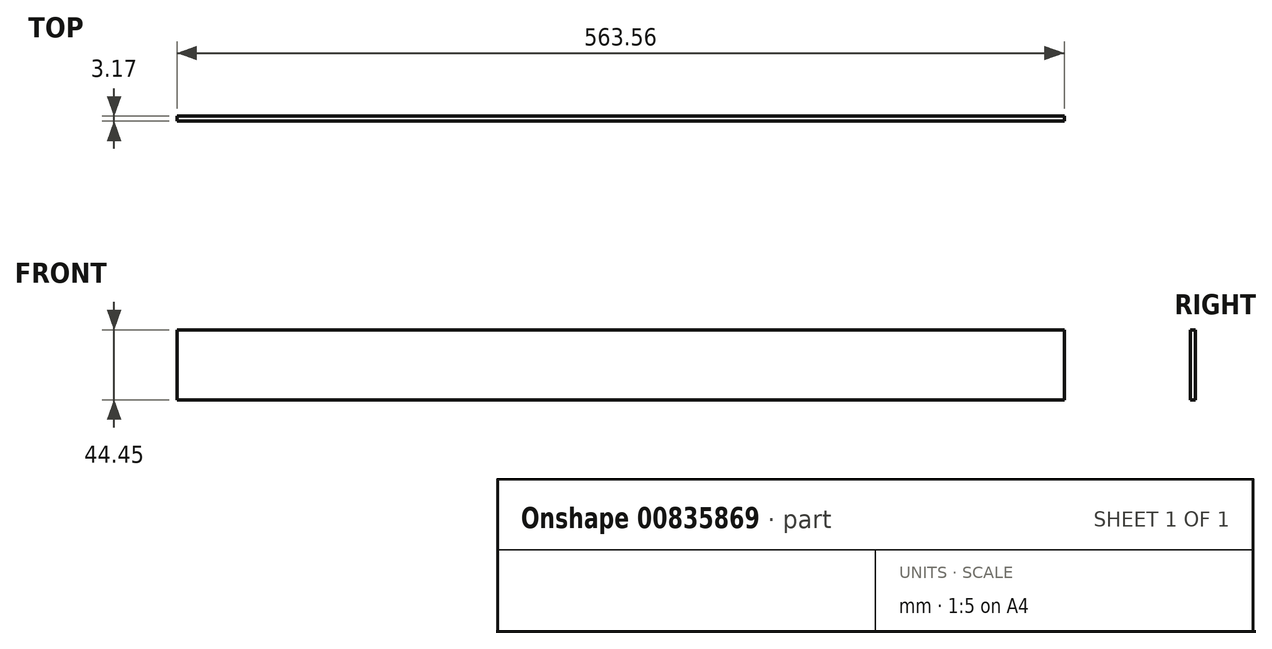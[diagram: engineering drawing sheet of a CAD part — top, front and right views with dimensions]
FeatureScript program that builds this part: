
annotation { "Feature Type Name" : "Feature", "Feature Type Description" : "" }
export const myFeature = defineFeature(function(context is Context, id is Id, definition is map)
    precondition{}
    {
        {
            var Q0;
            Q0=qCreatedBy(makeId("Right.planeOp"),FACE);
            var sketch = newSketch(context, id + "F0", { "sketchPlane" : qUnion([Q0])});
            skLineSegment(sketch, "E0.bottom", {"start": v(0, 0) * mm, "end": v(3.18, 0) * mm});
            skLineSegment(sketch, "E0.top", {"start": v(0, 44.45) * mm, "end": v(3.17, 44.45) * mm});
            skLineSegment(sketch, "E0.left", {"start": v(0, 0) * mm, "end": v(0, 44.45) * mm});
            skLineSegment(sketch, "E0.right", {"start": v(3.18, 0) * mm, "end": v(3.17, 44.45) * mm});
            skSolve(sketch);
        }
        {
            var Q0;
            Q0 = qSketchRegion(id + "F0", true);
            extrude(context, id + "F1", {"entities" : qUnion([Q0]), "depth" : 563.56 * mm, "offsetDistance" : 25.4 * mm});
        }
    });
